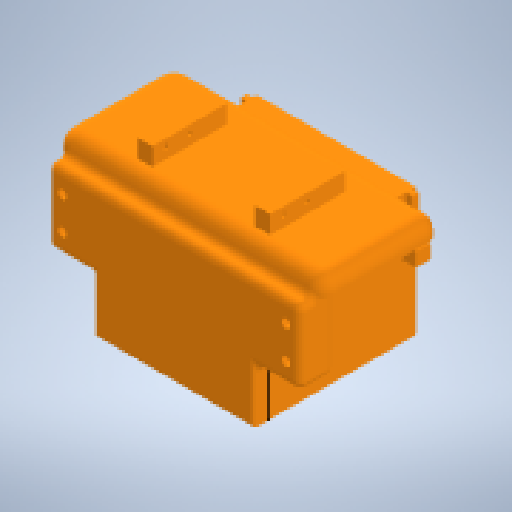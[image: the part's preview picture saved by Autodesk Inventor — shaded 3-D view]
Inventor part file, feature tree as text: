
AUTODESK INVENTOR PART (.ipt)
format: ipt  version: 2024.2 (Build 282272000, 272)  size: 691,712 bytes
history: native  units: mm
features: extrude x8, sketch x7, other x4, fillet x4
ambient origin geometry x8: Origin, YZ Plane, XZ Plane, XY Plane, X Axis, Y Axis, Z Axis, Center Point
bodies: Body1 (feature_tree)
feature tree (23):
  other  "Bryła1"
  sketch  "Szkic1"
  extrude  "Wyciągnięcie proste1"  Depth=93.0mm
  extrude  "Wyciągnięcie proste2"  Depth=72.0mm
  fillet  "Zaokrąglenie1"  Radius=107.0mm
  extrude  "Wyciągnięcie proste4"  Depth=86.0mm
  extrude  "Wyciągnięcie proste5"  Depth=10.0mm TaperAngle=0.0deg
  fillet  "Zaokrąglenie2"  Radius=100.0mm
  extrude  "Wyciągnięcie proste6"  Depth=2.0mm
  fillet  "Zaokrąglenie3"  Radius=5.0mm
  extrude  "Wyciągnięcie proste7"  Depth=5.0mm
  fillet  "Zaokrąglenie4"  Radius=92.0mm
  extrude  "Wyciągnięcie proste8"  Depth=53.0mm
  extrude  "Wyciągnięcie proste9"  Depth=28.0mm TaperAngle=0.0deg
  sketch  "Szkic3"
  sketch  "Szkic4"
  sketch  "Szkic6"
  sketch  "Szkic7"
  sketch  "Szkic8"
  sketch  "Szkic9"
  other  "Finish1"
  other  "Finish2"
  other  "Finish3"
